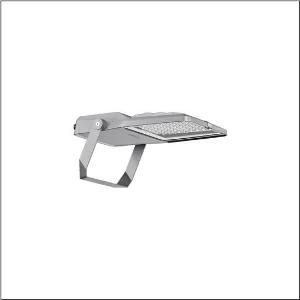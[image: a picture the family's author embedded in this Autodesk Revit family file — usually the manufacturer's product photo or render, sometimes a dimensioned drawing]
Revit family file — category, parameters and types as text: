
# Revit family: floodlight_fl_21_iq_mini___pl61_5xa7771d4c1a_f1b8
name_source: partatom
category: Lighting Fixtures
units: mm (PartAtom-declared; Revit-internal decimal feet)

## family parameters
Cut with Voids When Loaded = No
Host = Face
Light Source = No
Part Type = Normal
Room Calculation Point = No
Round Connector Dimension = Use Diameter
Shared = No

## types (1)
- --- (1 x LED, 18260 lm, 143 W, 4000K)
    Apparent Load = 143 VA
    CIE Flux Codes = 33 65 98 100 100
    Color Rendering = 70
    Color Temperature = 4000K
    Default Elevation = 1800 mm
    Description = Floodlight FL 21 iQ mini, floodlight, primary light control with lens, of PMMA, primary optical cover: protective disc, of toughened safety glass, transparent, light distribution: PL61, light emission: direct distribution, installation type: surface-mounted, lamps: LED, High Power LED, rated values: 18.260lm | 143W | 127,7lm/W (begin service life); end service life: 18.260lm | 151,6W; at 50% lumin. flux: 9.130lm | 60,8W | 150,2lm/W, colour temperature: 4000K, colour rendering: CRI > 70, light colour: 740, light setting 1 begin service life: 100% | 18.260lm | 143W | 127,7lm/W | 4.000K, light setting 1 end service life: 151,6W, further light settings possible, control: Auto-Match, Temp-Guard, Lumen-Switch, Night-Set, Smart-Wire, Light-Fading, Desk-Remote (wireless, voltage-free reading and setting of iQ features in the workshop via application-optimized NFC function/RFID function), optimised constant luminous flux control (CLO 2.0), pre-setting: linear dimming characteristic, with terminal, 6-pole, mains connection: 220..240V, AC, 50/60Hz, luminaire housing, of diecast aluminium, powder-coated, SITECO metallic grey (DB 702S), corrosivity category C5 mid according to DIN EN ISO 12944suitable for swimming poolschlorine-resistant, sealing non-destructively replaceable, mounting bracket, of steel, galvanised, powder-coated, SITECO metallic grey (DB 702S), protection rating (complete): IP66, insulation class (complete): insulation class II (safety insulation), certification: CE, ENEC, VDE, protection symbol: D, impact resistance: IK08, permissible operating ambient temperature: -40..+40°C, permissible operating ambient temperature for outdoor applications: -40..+50°C, standard: DIN EN 12944, LABS conformity tested according to VDMA 24364:2018-05, packaging unit: 1 piece

Light Distribution: PL61
    Height = 70 mm
    Lamp = 1 x LED
    Lamp Light Flux = 18260 lm
    Lamp Power = 143 W
    Lamp count = 1
    Length = 485 mm
    Luminous efficacy = 128 lm/W
    Manufacturer = Siteco
    ModVariant = No
    Model = 5XA7771D4C1A
    Mounting Place = Pole
    Mounting Type = Pole annexe
    Number of Poles = 1
    OnlyDefault = Yes
    Power Factor = 1
    Product Name = Floodlight FL 21 iQ mini | PL61
    Product group = floodlight | pylon annexe
    ProductGroupID = 6201
    Protection Class = Protection class II
    Protection Degree = IP 66
    RLX_Detail_Level = 1
    RLX_Emergency_Light_Flux = 0 lm
    RLX_Emergency_Type = 0
    RLX_Emergency_Type_DB = No
    RlxData = <blob elided: 97037 chars, md5=3a281005>
    Socket = socket
    Standby Power = 0 W
    System Light Flux = 18260 lm
    System Power = 143 W
    Type Comments = factory setting: luminous flux: 100 % | dim-lin: 254 | 730 mA
    Type Image = l_1006845.jpg
    URL = http://relux.com
    VarID = @adj_173721
    Voltage = 0 V
    Weight = 0.00 kg
    Width = 337 mm

## geometry (parser evidence)
native form markers: Blend x4, Sweep x13
no freeform markers — native parametric forms only
